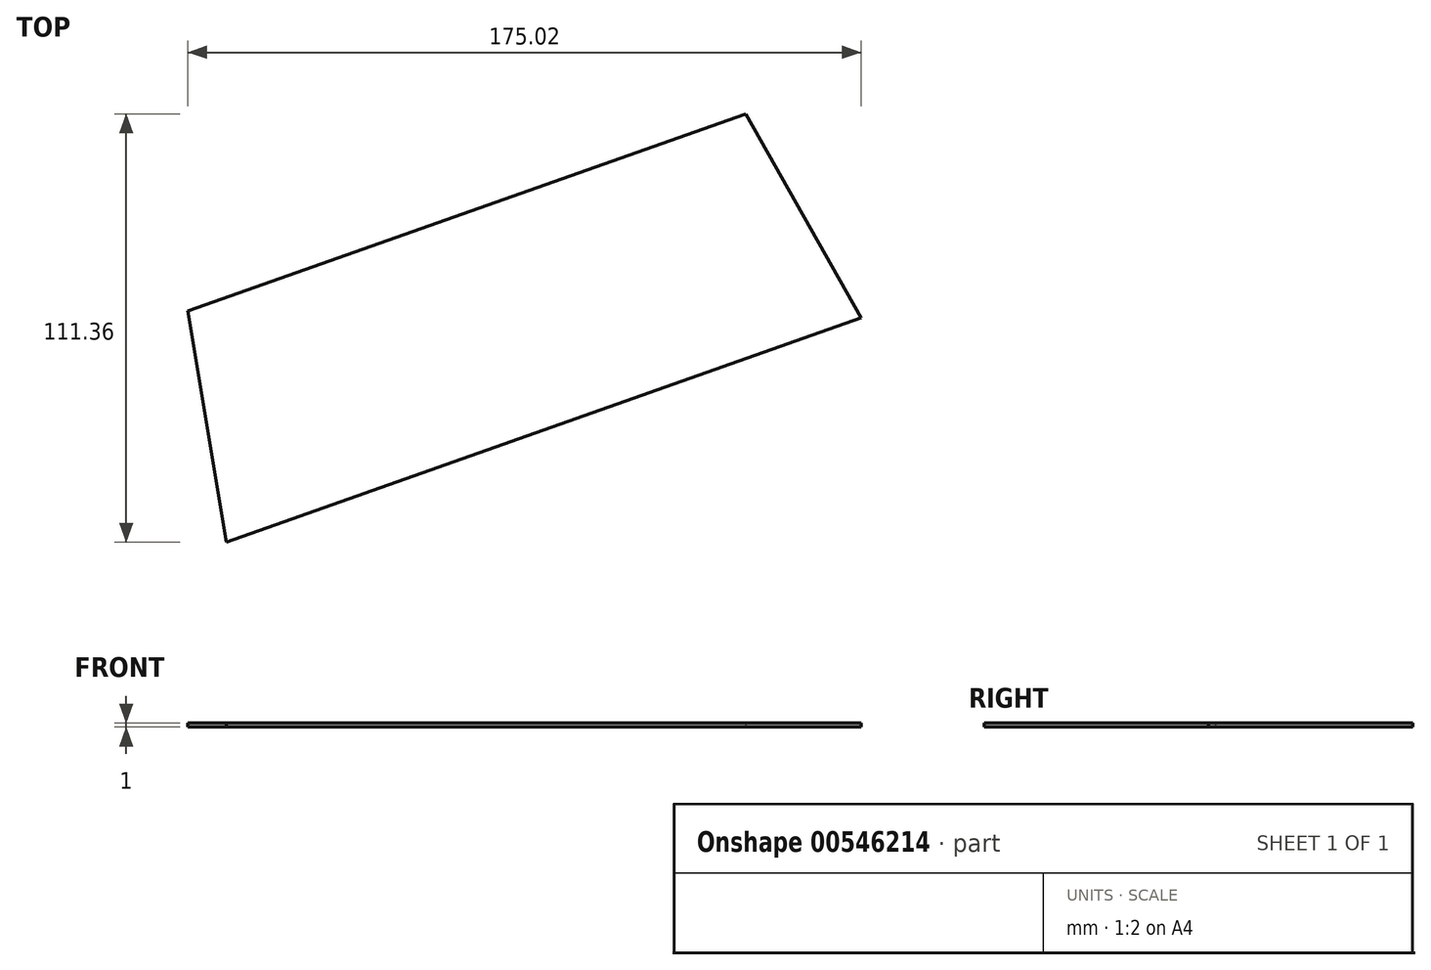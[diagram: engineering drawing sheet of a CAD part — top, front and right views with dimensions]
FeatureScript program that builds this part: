
annotation { "Feature Type Name" : "Feature", "Feature Type Description" : "" }
export const myFeature = defineFeature(function(context is Context, id is Id, definition is map)
    precondition{}
    {
        {
            var Q0;
            Q0=qCreatedBy(makeId("Top.planeOp"),FACE);
            var sketch = newSketch(context, id + "F0", { "sketchPlane" : qUnion([Q0])});
            skLineSegment(sketch, "E0.bottom", {"start": v(-225, 148.5) * mm, "end": v(15, 148.5) * mm, "construction": true});
            skLineSegment(sketch, "E0.top", {"start": v(-225, -148.5) * mm, "end": v(15, -148.5) * mm, "construction": true});
            skLineSegment(sketch, "E0.left", {"start": v(-225, 148.5) * mm, "end": v(-225, -148.5) * mm, "construction": true});
            skLineSegment(sketch, "E0.right", {"start": v(15, 148.5) * mm, "end": v(15, -148.5) * mm, "construction": true});
            skLineSegment(sketch, "E1", {"start": v(-15, 148.5) * mm, "end": v(-15, -148.5) * mm, "construction": true});
            skLineSegment(sketch, "E2", {"start": v(0, 148.5) * mm, "end": v(0, -148.5) * mm, "construction": true});
            skSolve(sketch);
        }
        {
            var Q0;
            Q0=qCreatedBy(makeId("Top.planeOp"),FACE);
            var sketch = newSketch(context, id + "F1", { "sketchPlane" : qUnion([Q0])});
            skLineSegment(sketch, "E3", {"start": v(-165, 30.2) * mm, "end": v(0, 88.5) * mm});
            skLineSegment(sketch, "E4", {"start": v(-165, 30.2) * mm, "end": v(-175.02, 90.29) * mm});
            skLineSegment(sketch, "E5", {"start": v(-175.02, 90.29) * mm, "end": v(-29.97, 141.55) * mm});
            skLineSegment(sketch, "E6", {"start": v(-29.97, 141.55) * mm, "end": v(0, 88.5) * mm});
            skSolve(sketch);
        }
        {
            var Q0;
            Q0 = qSketchRegion(id + "F1", true);
            extrude(context, id + "F2", {"entities" : qUnion([Q0]), "depth" : 1 * mm, "offsetDistance" : 25 * mm});
        }
    });
